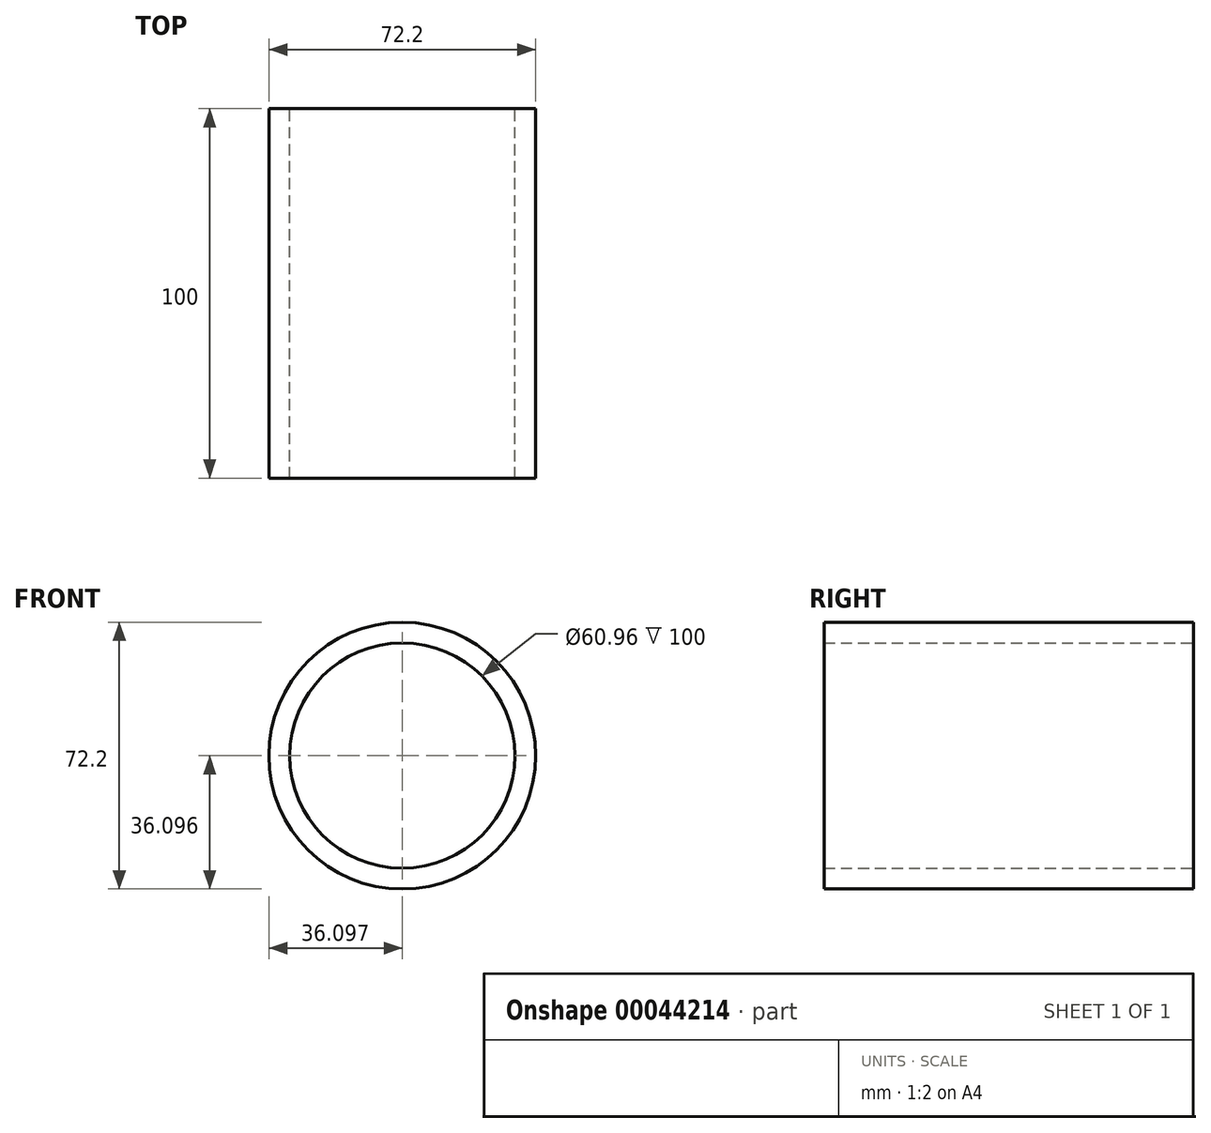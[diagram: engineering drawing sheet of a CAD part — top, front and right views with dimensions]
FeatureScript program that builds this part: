
annotation { "Feature Type Name" : "Feature", "Feature Type Description" : "" }
export const myFeature = defineFeature(function(context is Context, id is Id, definition is map)
    precondition{}
    {
        {
            var Q0;
            Q0=qCreatedBy(makeId("Front.planeOp"),FACE);
            var sketch = newSketch(context, id + "F0", { "sketchPlane" : qUnion([Q0])});
            skCircle(sketch, "E0", {"center": v(11.35, -9.28) * mm, "radius": 30.48 * mm});
            skCircle(sketch, "E1", {"center": v(11.35, -9.28) * mm, "radius": 36.1 * mm});
            skSolve(sketch);
        }
        {
            var Q0;
            Q0=makeQuery(id+"F0.imprint","IMPRINT",FACE,{"disambiguationData":[TD([[makeQuery(id+"F0.imprint","IMPRINT",EDGE,{"derivedFrom":sQuery(id+"F0.wireOp",EDGE,"E0")}),-1.0]])]});
            extrude(context, id + "F1", {"entities" : qUnion([Q0]), "depth" : 100 * mm});
        }
    });
